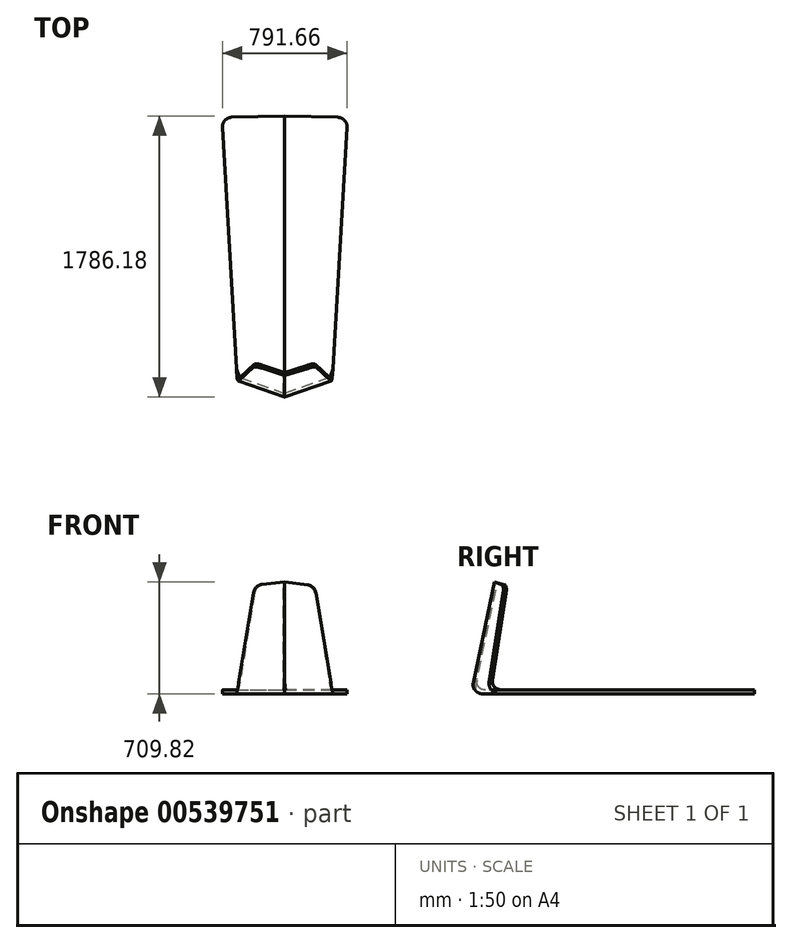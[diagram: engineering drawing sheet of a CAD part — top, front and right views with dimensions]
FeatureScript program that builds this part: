
annotation { "Feature Type Name" : "Feature", "Feature Type Description" : "" }
export const myFeature = defineFeature(function(context is Context, id is Id, definition is map)
    precondition{}
    {
        {
            var Q0;
            Q0=qCreatedBy(makeId("Top.planeOp"),FACE);
            var sketch = newSketch(context, id + "F0", { "sketchPlane" : qUnion([Q0])});
            skLineSegment(sketch, "E0", {"start": v(0, 587.82) * mm, "end": v(0, -1212.18) * mm});
            skLineSegment(sketch, "E1", {"start": v(0, -1212.18) * mm, "end": v(-300, -1107.97) * mm});
            skLineSegment(sketch, "E2", {"start": v(-300, -1107.97) * mm, "end": v(-400, 587.82) * mm});
            skLineSegment(sketch, "E3", {"start": v(-400, 587.82) * mm, "end": v(0, 587.82) * mm});
            skSolve(sketch);
        }
        {
            var Q0;
            Q0 = qSketchRegion(id + "F0", true);
            extrude(context, id + "F1", {"entities" : qUnion([Q0]), "depth" : 25 * mm, "offsetDistance" : 25 * mm});
        }
        {
            var Q0;
            Q0=makeQuery(id+"F1.opExtrude","CAP_EDGE",EDGE,{"disambiguationData":[OSD([sQuery(id+"F0.wireOp",EDGE,"E1")])],"isStart":false});
            chamfer(context, id + "F2", {"entities" : qUnion([Q0]), "chamferType" : ChamferType.TWO_OFFSETS, "width1" : 25 * mm, "oppositeDirection" : false, "width2" : 5 * mm, "tangentPropagation" : true});
        }
        {
            var Q0;
            Q0=makeQuery(id+"F2.opChamfer","BLEND_FACE",FACE,{"disambiguationData":[OSD([sQuery(id+"F0.wireOp",EDGE,"E1")])]});
            var sketch = newSketch(context, id + "F3", { "sketchPlane" : qUnion([Q0])});
            skLineSegment(sketch, "E4", {"start": v(64.37, -203.92) * mm, "end": v(381.56, -225.52) * mm});
            skLineSegment(sketch, "E5", {"start": v(381.56, -225.52) * mm, "end": v(381.56, 474.48) * mm});
            skLineSegment(sketch, "E6", {"start": v(381.56, 474.48) * mm, "end": v(181.56, 474.48) * mm});
            skLineSegment(sketch, "E7", {"start": v(181.56, 474.48) * mm, "end": v(64.37, -203.92) * mm});
            skSolve(sketch);
        }
        {
            var Q0;
            Q0=makeQuery(id+"F3.imprint","IMPRINT",FACE,{"disambiguationData":[TD([[makeQuery(id+"F3.imprint","IMPRINT",EDGE,{"derivedFrom":sQuery(id+"F3.wireOp",EDGE,"E4")}),1.0]])]});
            extrude(context, id + "F4", {"entities" : qUnion([Q0]), "operationType" : NewBodyOperationType.ADD, "oppositeDirection" : true, "depth" : 20 * mm, "offsetDistance" : 25 * mm});
        }
        {
            var Q0;
            Q0=makeQuery(id+"F1.opExtrude","SWEPT_BODY",BODY,{"disambiguationData":[OSD([sQuery(id+"F0.wireOp",EDGE,"E0"),sQuery(id+"F0.wireOp",EDGE,"E1"),sQuery(id+"F0.wireOp",EDGE,"E2"),sQuery(id+"F0.wireOp",EDGE,"E3")])]});
            var Q1;
            Q1=makeQuery(id+"F1.opExtrude","SWEPT_FACE",FACE,{"disambiguationData":[OSD([sQuery(id+"F0.wireOp",EDGE,"E0")])]});
            var Q2;
            Q2=qCreatedBy(makeId("Right.planeOp"),FACE);
            mirror(context, id + "F5", {"entities" : qUnion([Q0]), "faces" : qUnion([Q1]), "mirrorPlane" : qUnion([Q2])});
        }
        {
            var Q0;
            Q0=makeQuery(id+"F5.opPattern","COPY",EDGE,{"derivedFrom":makeQuery(id+"F4.boolean.opBoolean","INTERSECT",EDGE,{"derivedFrom":[makeQuery(id+"F1.opExtrude","CAP_FACE",FACE,{"disambiguationData":[OSD([sQuery(id+"F0.wireOp",EDGE,"E0"),sQuery(id+"F0.wireOp",EDGE,"E1"),sQuery(id+"F0.wireOp",EDGE,"E2"),sQuery(id+"F0.wireOp",EDGE,"E3")])],"isStart":false}),makeQuery(id+"F4.opExtrude","CAP_FACE",FACE,{"disambiguationData":[OSD([sQuery(id+"F3.wireOp",EDGE,"E4"),sQuery(id+"F3.wireOp",EDGE,"E5"),sQuery(id+"F3.wireOp",EDGE,"E6"),sQuery(id+"F3.wireOp",EDGE,"E7")])],"isStart":false})]}),"instanceName":"1"});
            var Q1;
            Q1=makeQuery(id+"F4.boolean.opBoolean","INTERSECT",EDGE,{"derivedFrom":[makeQuery(id+"F1.opExtrude","CAP_FACE",FACE,{"disambiguationData":[OSD([sQuery(id+"F0.wireOp",EDGE,"E0"),sQuery(id+"F0.wireOp",EDGE,"E1"),sQuery(id+"F0.wireOp",EDGE,"E2"),sQuery(id+"F0.wireOp",EDGE,"E3")])],"isStart":false}),makeQuery(id+"F4.opExtrude","CAP_FACE",FACE,{"disambiguationData":[OSD([sQuery(id+"F3.wireOp",EDGE,"E4"),sQuery(id+"F3.wireOp",EDGE,"E5"),sQuery(id+"F3.wireOp",EDGE,"E6"),sQuery(id+"F3.wireOp",EDGE,"E7")])],"isStart":false})]});
            fillet(context, id + "F6", {"entities" : qUnion([Q0, Q1]), "radius" : 50 * mm, "tangentPropagation" : true, "allowEdgeOverflow" : false});
        }
        {
            var Q0;
            {var subQ0=sQuery(id+"F0.wireOp",EDGE,"E1");Q0=makeQuery(id+"F5.opPattern","COPY",EDGE,{"derivedFrom":makeQuery(id+"F2.opChamfer","BLEND_EDGE",EDGE,{"blendedFrom":[makeQuery(id+"F1.opExtrude","CAP_EDGE",EDGE,{"disambiguationData":[OSD([subQ0])],"isStart":false}),makeQuery(id+"F1.opExtrude","CAP_FACE",FACE,{"disambiguationData":[OSD([sQuery(id+"F0.wireOp",EDGE,"E0"),subQ0,sQuery(id+"F0.wireOp",EDGE,"E2"),sQuery(id+"F0.wireOp",EDGE,"E3")])],"isStart":true})],"blendedInto":[makeQuery(id+"F1.opExtrude","CAP_FACE",FACE,{"disambiguationData":[OSD([sQuery(id+"F0.wireOp",EDGE,"E0"),subQ0,sQuery(id+"F0.wireOp",EDGE,"E2"),sQuery(id+"F0.wireOp",EDGE,"E3")])],"isStart":true})]}),"instanceName":"1"});}
            var Q1;
            {var subQ0=sQuery(id+"F0.wireOp",EDGE,"E1");Q1=makeQuery(id+"F2.opChamfer","BLEND_EDGE",EDGE,{"blendedFrom":[makeQuery(id+"F1.opExtrude","CAP_EDGE",EDGE,{"disambiguationData":[OSD([subQ0])],"isStart":false}),makeQuery(id+"F1.opExtrude","CAP_FACE",FACE,{"disambiguationData":[OSD([sQuery(id+"F0.wireOp",EDGE,"E0"),subQ0,sQuery(id+"F0.wireOp",EDGE,"E2"),sQuery(id+"F0.wireOp",EDGE,"E3")])],"isStart":true})],"blendedInto":[makeQuery(id+"F1.opExtrude","CAP_FACE",FACE,{"disambiguationData":[OSD([sQuery(id+"F0.wireOp",EDGE,"E0"),subQ0,sQuery(id+"F0.wireOp",EDGE,"E2"),sQuery(id+"F0.wireOp",EDGE,"E3")])],"isStart":true})]});}
            fillet(context, id + "F7", {"entities" : qUnion([Q0, Q1]), "radius" : 60 * mm, "tangentPropagation" : true, "allowEdgeOverflow" : false});
        }
        {
            var Q0;
            Q0=makeQuery(id+"F5.opPattern","COPY",EDGE,{"derivedFrom":makeQuery(id+"F4.opExtrude","SWEPT_EDGE",EDGE,{"disambiguationData":[OSD([sQuery(id+"F3.wireOp",EDGE,"E6"),sQuery(id+"F3.wireOp",EDGE,"E7")])]}),"instanceName":"1"});
            chamfer(context, id + "F8", {"entities" : qUnion([Q0]), "chamferType" : ChamferType.TWO_OFFSETS, "width1" : 10 * mm, "oppositeDirection" : false, "width2" : 200 * mm});
        }
        {
            var Q0;
            Q0=makeQuery(id+"F4.opExtrude","SWEPT_EDGE",EDGE,{"disambiguationData":[OSD([sQuery(id+"F3.wireOp",EDGE,"E6"),sQuery(id+"F3.wireOp",EDGE,"E7")])]});
            chamfer(context, id + "F9", {"entities" : qUnion([Q0]), "chamferType" : ChamferType.TWO_OFFSETS, "width1" : 200 * mm, "oppositeDirection" : false, "width2" : 5 * mm, "tangentPropagation" : true});
        }
        {
            var Q0;
            {var subQ0=sQuery(id+"F3.wireOp",EDGE,"E7");Q0=makeQuery(id+"F9.opChamfer","BLEND_EDGE",EDGE,{"blendedFrom":[makeQuery(id+"F4.opExtrude","SWEPT_EDGE",EDGE,{"disambiguationData":[OSD([sQuery(id+"F3.wireOp",EDGE,"E6"),subQ0])]}),makeQuery(id+"F4.opExtrude","SWEPT_FACE",FACE,{"disambiguationData":[OSD([subQ0])]})],"blendedInto":[makeQuery(id+"F4.opExtrude","SWEPT_FACE",FACE,{"disambiguationData":[OSD([subQ0])]})]});}
            var Q1;
            {var subQ0=sQuery(id+"F3.wireOp",EDGE,"E7");Q1=makeQuery(id+"F8.opChamfer","BLEND_EDGE",EDGE,{"blendedFrom":[makeQuery(id+"F5.opPattern","COPY",EDGE,{"derivedFrom":makeQuery(id+"F4.opExtrude","SWEPT_EDGE",EDGE,{"disambiguationData":[OSD([sQuery(id+"F3.wireOp",EDGE,"E6"),subQ0])]}),"instanceName":"1"}),makeQuery(id+"F5.opPattern","COPY",FACE,{"derivedFrom":makeQuery(id+"F4.opExtrude","SWEPT_FACE",FACE,{"disambiguationData":[OSD([subQ0])]}),"instanceName":"1"})],"blendedInto":[makeQuery(id+"F5.opPattern","COPY",FACE,{"derivedFrom":makeQuery(id+"F4.opExtrude","SWEPT_FACE",FACE,{"disambiguationData":[OSD([subQ0])]}),"instanceName":"1"})]});}
            fillet(context, id + "F10", {"entities" : qUnion([Q0, Q1]), "radius" : 58.5 * mm, "tangentPropagation" : true, "allowEdgeOverflow" : false});
        }
        {
            var Q0;
            Q0=makeQuery(id+"F5.opPattern","COPY",EDGE,{"derivedFrom":makeQuery(id+"F1.opExtrude","SWEPT_EDGE",EDGE,{"disambiguationData":[OSD([sQuery(id+"F0.wireOp",EDGE,"E2"),sQuery(id+"F0.wireOp",EDGE,"E3")])]}),"instanceName":"1"});
            chamfer(context, id + "F11", {"entities" : qUnion([Q0]), "chamferType" : ChamferType.TWO_OFFSETS, "width1" : 400 * mm, "oppositeDirection" : false, "width2" : 10 * mm, "tangentPropagation" : true});
        }
        {
            var Q0;
            Q0=makeQuery(id+"F1.opExtrude","SWEPT_EDGE",EDGE,{"disambiguationData":[OSD([sQuery(id+"F0.wireOp",EDGE,"E2"),sQuery(id+"F0.wireOp",EDGE,"E3")])]});
            chamfer(context, id + "F12", {"entities" : qUnion([Q0]), "chamferType" : ChamferType.TWO_OFFSETS, "width1" : 10 * mm, "oppositeDirection" : false, "width2" : 400 * mm, "tangentPropagation" : true});
        }
        {
            var Q0;
            {var subQ0=sQuery(id+"F0.wireOp",EDGE,"E2");Q0=makeQuery(id+"F11.opChamfer","BLEND_EDGE",EDGE,{"blendedFrom":[makeQuery(id+"F5.opPattern","COPY",EDGE,{"derivedFrom":makeQuery(id+"F1.opExtrude","SWEPT_EDGE",EDGE,{"disambiguationData":[OSD([subQ0,sQuery(id+"F0.wireOp",EDGE,"E3")])]}),"instanceName":"1"}),makeQuery(id+"F5.opPattern","COPY",FACE,{"derivedFrom":makeQuery(id+"F1.opExtrude","SWEPT_FACE",FACE,{"disambiguationData":[OSD([subQ0])]}),"instanceName":"1"})],"blendedInto":[makeQuery(id+"F5.opPattern","COPY",FACE,{"derivedFrom":makeQuery(id+"F1.opExtrude","SWEPT_FACE",FACE,{"disambiguationData":[OSD([subQ0])]}),"instanceName":"1"})]});}
            var Q1;
            {var subQ0=sQuery(id+"F0.wireOp",EDGE,"E2");Q1=makeQuery(id+"F12.opChamfer","BLEND_EDGE",EDGE,{"blendedFrom":[makeQuery(id+"F1.opExtrude","SWEPT_EDGE",EDGE,{"disambiguationData":[OSD([subQ0,sQuery(id+"F0.wireOp",EDGE,"E3")])]}),makeQuery(id+"F1.opExtrude","SWEPT_FACE",FACE,{"disambiguationData":[OSD([subQ0])]})],"blendedInto":[makeQuery(id+"F1.opExtrude","SWEPT_FACE",FACE,{"disambiguationData":[OSD([subQ0])]})]});}
            fillet(context, id + "F13", {"entities" : qUnion([Q0, Q1]), "radius" : 60.52 * mm, "tangentPropagation" : true, "allowEdgeOverflow" : false});
        }
        {
            var Q0;
            Q0=makeQuery(id+"F5.opPattern","COPY",EDGE,{"derivedFrom":makeQuery(id+"F4.boolean.opBoolean","INTERSECT",EDGE,{"derivedFrom":[makeQuery(id+"F1.opExtrude","CAP_FACE",FACE,{"disambiguationData":[OSD([sQuery(id+"F0.wireOp",EDGE,"E0"),sQuery(id+"F0.wireOp",EDGE,"E1"),sQuery(id+"F0.wireOp",EDGE,"E2"),sQuery(id+"F0.wireOp",EDGE,"E3")])],"isStart":false}),makeQuery(id+"F4.opExtrude","SWEPT_FACE",FACE,{"disambiguationData":[OSD([sQuery(id+"F3.wireOp",EDGE,"E7")])]})]}),"instanceName":"1"});
            var Q1;
            Q1=makeQuery(id+"F4.boolean.opBoolean","INTERSECT",EDGE,{"derivedFrom":[makeQuery(id+"F1.opExtrude","CAP_FACE",FACE,{"disambiguationData":[OSD([sQuery(id+"F0.wireOp",EDGE,"E0"),sQuery(id+"F0.wireOp",EDGE,"E1"),sQuery(id+"F0.wireOp",EDGE,"E2"),sQuery(id+"F0.wireOp",EDGE,"E3")])],"isStart":false}),makeQuery(id+"F4.opExtrude","SWEPT_FACE",FACE,{"disambiguationData":[OSD([sQuery(id+"F3.wireOp",EDGE,"E7")])]})]});
            fillet(context, id + "F14", {"entities" : qUnion([Q0, Q1]), "radius" : 74.31 * mm, "tangentPropagation" : true, "allowEdgeOverflow" : false});
        }
    });
